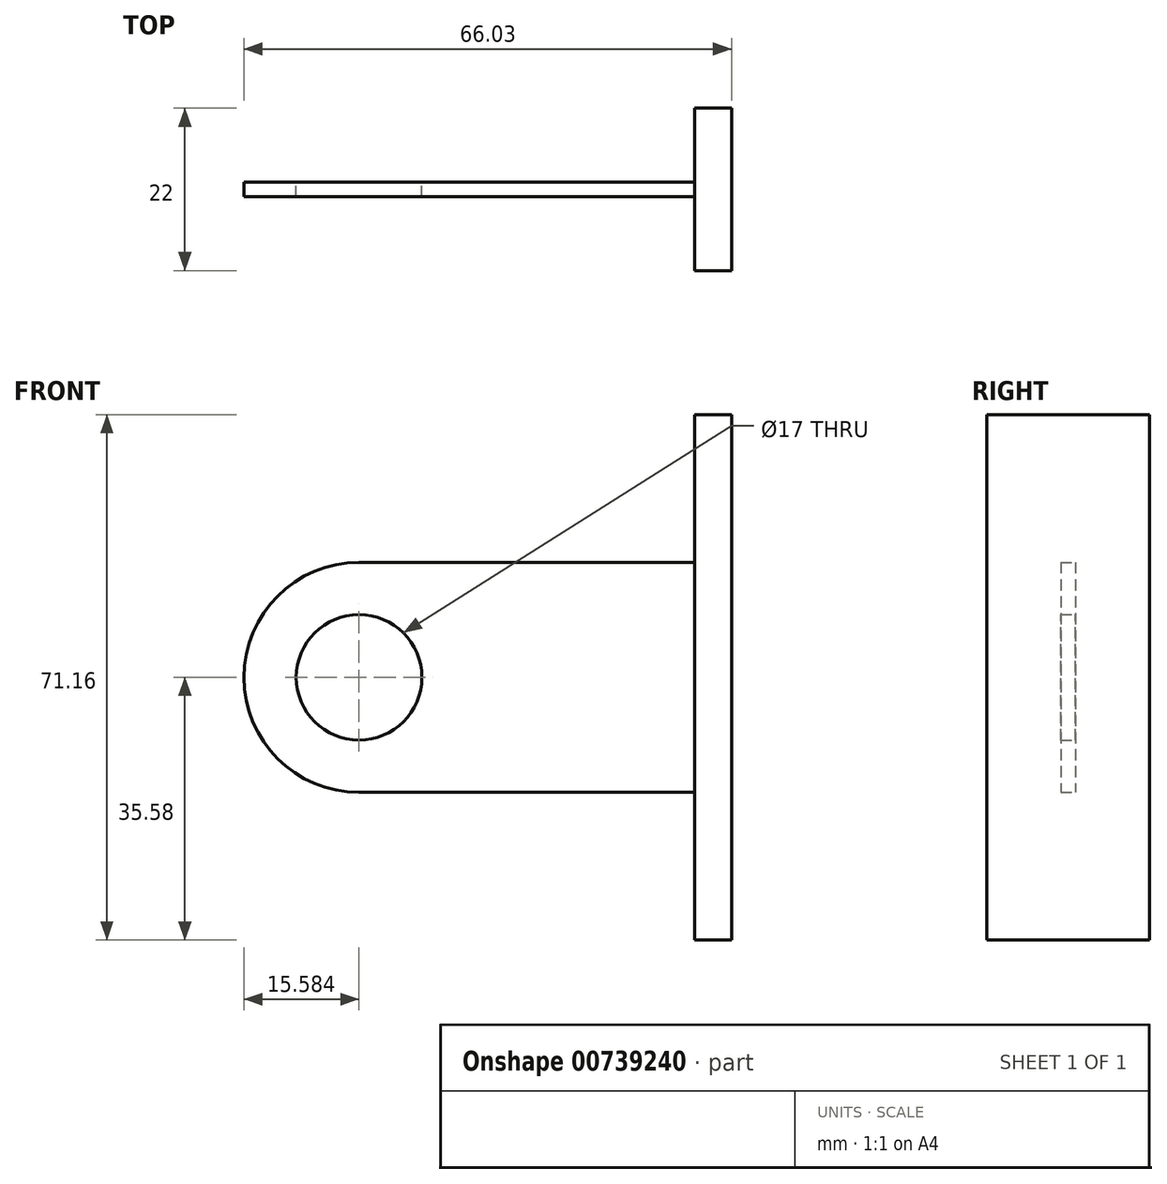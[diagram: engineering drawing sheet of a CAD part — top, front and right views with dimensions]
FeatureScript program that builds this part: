
annotation { "Feature Type Name" : "Feature", "Feature Type Description" : "" }
export const myFeature = defineFeature(function(context is Context, id is Id, definition is map)
    precondition{}
    {
        {
            var Q0;
            Q0=qCreatedBy(makeId("Front.planeOp"),FACE);
            var sketch = newSketch(context, id + "F0", { "sketchPlane" : qUnion([Q0])});
            skLineSegment(sketch, "E0", {"start": v(-19.2, 16.62) * mm, "end": v(26.24, 16.62) * mm});
            skLineSegment(sketch, "E1", {"start": v(26.24, -14.54) * mm, "end": v(-19.2, -14.54) * mm});
            skArc(sketch, "E2", {"start": v(-19.2, 16.62) * mm, "mid": v(-34.79, 1.04) * mm, "end": v(-19.2, -14.54) * mm});
            skLineSegment(sketch, "E3", {"start": v(26.24, 16.62) * mm, "end": v(26.24, -14.54) * mm});
            skCircle(sketch, "E4", {"center": v(-19.2, 1.04) * mm, "radius": 8.5 * mm});
            skSolve(sketch);
        }
        {
            var Q0;
            Q0 = qSketchRegion(id + "F0", true);
            extrude(context, id + "F1", {"entities" : qUnion([Q0]), "depth" : 2 * mm, "offsetDistance" : 25.4 * mm});
        }
        {
            var Q0;
            Q0=makeQuery(id+"F1.opExtrude","SWEPT_FACE",FACE,{"disambiguationData":[OSD([sQuery(id+"F0.wireOp",EDGE,"E3")])]});
            var sketch = newSketch(context, id + "F2", { "sketchPlane" : qUnion([Q0])});
            skLineSegment(sketch, "E5.bottom", {"start": v(-12, 36.62) * mm, "end": v(10, 36.62) * mm});
            skLineSegment(sketch, "E5.top", {"start": v(-12, -34.54) * mm, "end": v(10, -34.54) * mm});
            skLineSegment(sketch, "E5.left", {"start": v(-12, 36.62) * mm, "end": v(-12, -34.54) * mm});
            skLineSegment(sketch, "E5.right", {"start": v(10, 36.62) * mm, "end": v(10, -34.54) * mm});
            skSolve(sketch);
        }
        {
            var Q0;
            Q0 = qSketchRegion(id + "F2", true);
            extrude(context, id + "F3", {"entities" : qUnion([Q0]), "operationType" : NewBodyOperationType.ADD, "depth" : 5 * mm, "offsetDistance" : 25.4 * mm});
        }
    });
